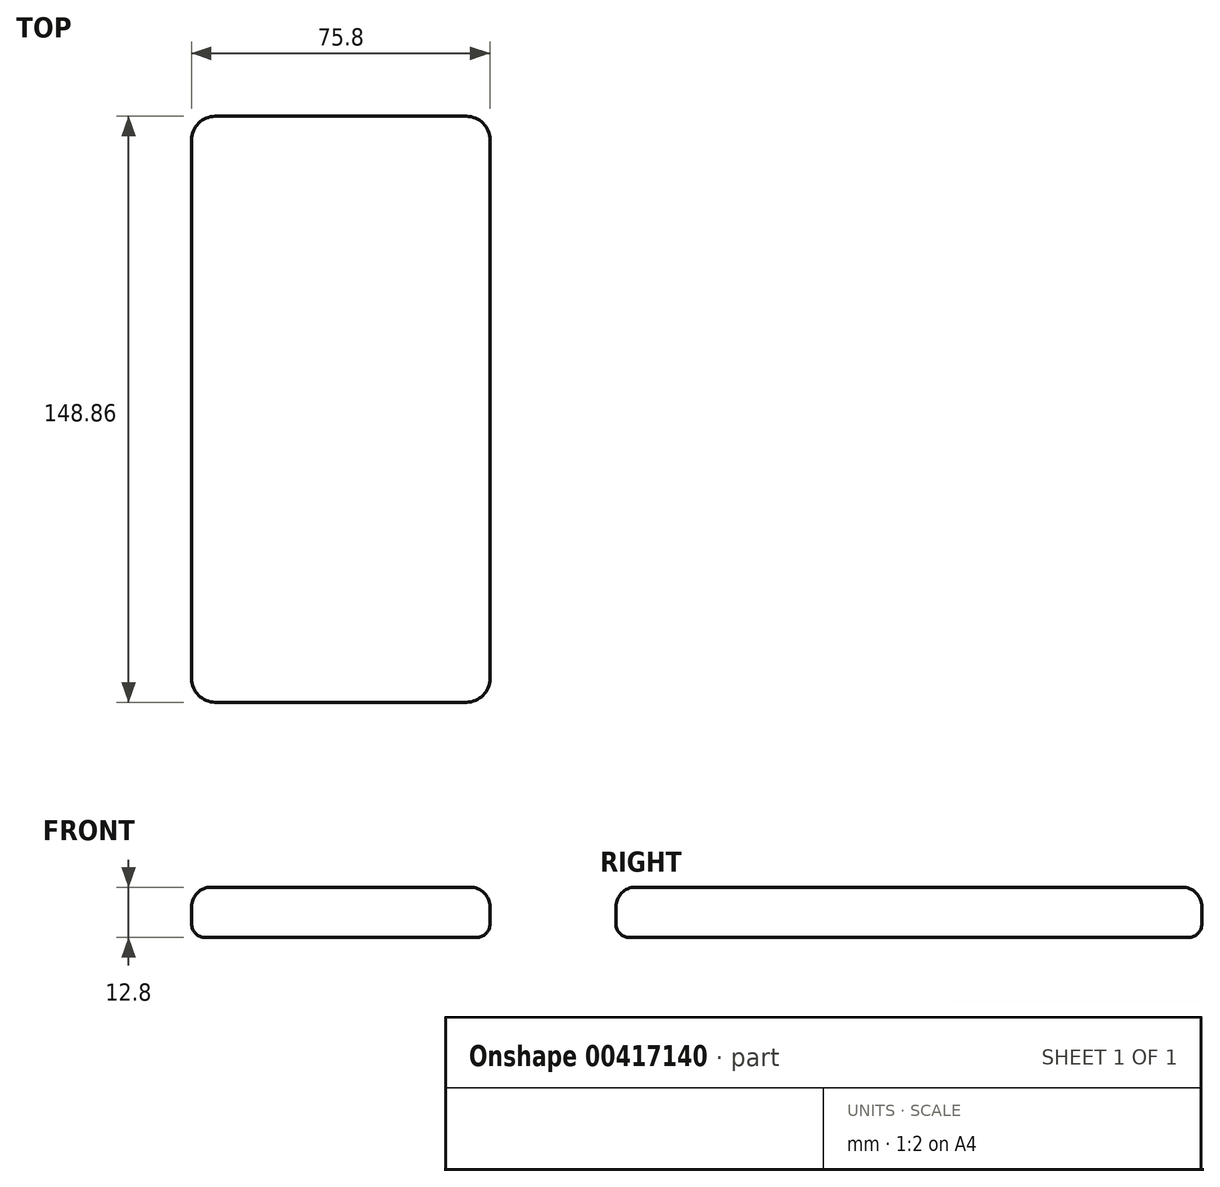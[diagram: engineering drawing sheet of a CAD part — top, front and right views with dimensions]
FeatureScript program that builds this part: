
annotation { "Feature Type Name" : "Feature", "Feature Type Description" : "" }
export const myFeature = defineFeature(function(context is Context, id is Id, definition is map)
    precondition{}
    {
        {
            var Q0;
            Q0=qCreatedBy(makeId("Top.planeOp"),FACE);
            var sketch = newSketch(context, id + "F0", { "sketchPlane" : qUnion([Q0])});
            skLineSegment(sketch, "E0.bottom", {"start": v(37.9, 74.43) * mm, "end": v(-37.9, 74.43) * mm});
            skLineSegment(sketch, "E0.top", {"start": v(37.9, -74.43) * mm, "end": v(-37.9, -74.43) * mm});
            skLineSegment(sketch, "E0.left", {"start": v(37.9, 74.43) * mm, "end": v(37.9, -74.43) * mm});
            skLineSegment(sketch, "E0.right", {"start": v(-37.9, 74.43) * mm, "end": v(-37.9, -74.43) * mm});
            skPoint(sketch, "E0.middle", {"position": v(0, 0) * mm});
            skSolve(sketch);
        }
        {
            var Q0;
            Q0 = qSketchRegion(id + "F0", true);
            extrude(context, id + "F1", {"entities" : qUnion([Q0]), "depth" : 12.8 * mm});
        }
        {
            var Q0;
            Q0=makeQuery(id+"F1.opExtrude","SWEPT_EDGE",EDGE,{"disambiguationData":[OSD([sQuery(id+"F0.wireOp",EDGE,"E0.bottom"),sQuery(id+"F0.wireOp",EDGE,"E0.left")])]});
            var Q1;
            Q1=makeQuery(id+"F1.opExtrude","SWEPT_EDGE",EDGE,{"disambiguationData":[OSD([sQuery(id+"F0.wireOp",EDGE,"E0.bottom"),sQuery(id+"F0.wireOp",EDGE,"E0.right")])]});
            var Q2;
            Q2=makeQuery(id+"F1.opExtrude","SWEPT_EDGE",EDGE,{"disambiguationData":[OSD([sQuery(id+"F0.wireOp",EDGE,"E0.top"),sQuery(id+"F0.wireOp",EDGE,"E0.right")])]});
            var Q3;
            Q3=makeQuery(id+"F1.opExtrude","SWEPT_EDGE",EDGE,{"disambiguationData":[OSD([sQuery(id+"F0.wireOp",EDGE,"E0.top"),sQuery(id+"F0.wireOp",EDGE,"E0.left")])]});
            fillet(context, id + "F2", {"entities" : qUnion([Q0, Q1, Q2, Q3]), "radius" : 6 * mm, "tangentPropagation" : true, "allowEdgeOverflow" : false});
        }
        {
            var Q0;
            Q0=makeQuery(id+"F1.opExtrude","CAP_EDGE",EDGE,{"disambiguationData":[OSD([sQuery(id+"F0.wireOp",EDGE,"E0.bottom")])],"isStart":true});
            fillet(context, id + "F3", {"entities" : qUnion([Q0]), "radius" : 3.5 * mm, "tangentPropagation" : true, "allowEdgeOverflow" : false});
        }
        {
            var Q0;
            Q0=makeQuery(id+"F1.opExtrude","CAP_EDGE",EDGE,{"disambiguationData":[OSD([sQuery(id+"F0.wireOp",EDGE,"E0.bottom")])],"isStart":false});
            fillet(context, id + "F4", {"entities" : qUnion([Q0]), "radius" : 5 * mm, "tangentPropagation" : true, "allowEdgeOverflow" : false});
        }
    });
